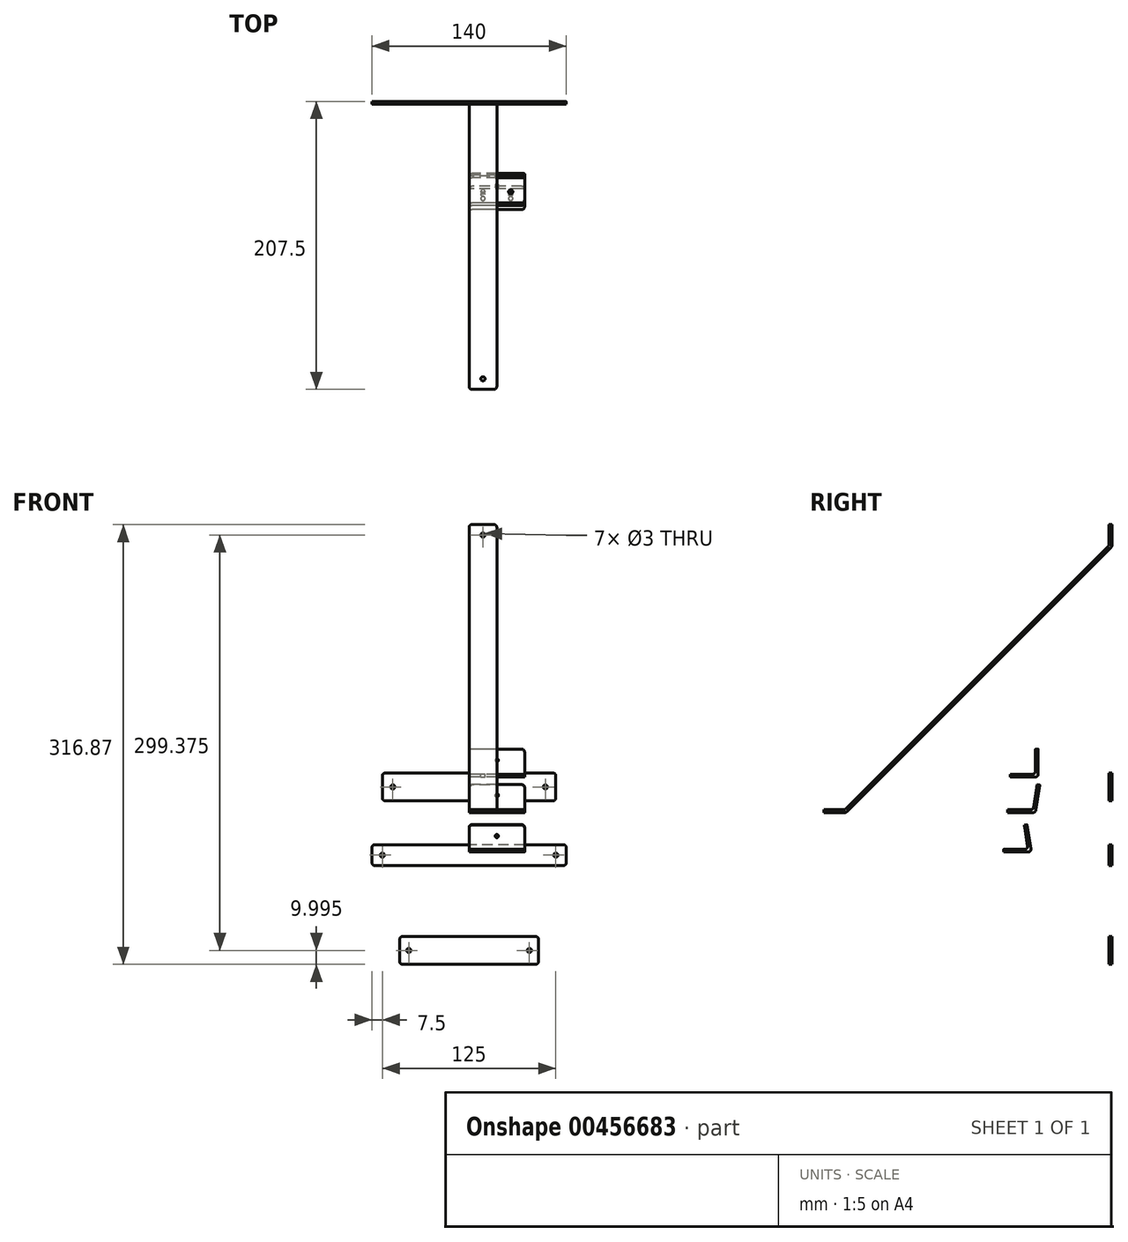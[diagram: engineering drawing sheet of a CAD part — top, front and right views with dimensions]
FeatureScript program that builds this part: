
annotation { "Feature Type Name" : "Feature", "Feature Type Description" : "" }
export const myFeature = defineFeature(function(context is Context, id is Id, definition is map)
    precondition{}
    {
        {
            var Q0;
            Q0=qCreatedBy(makeId("Front.planeOp"),FACE);
            var sketch = newSketch(context, id + "F0", { "sketchPlane" : qUnion([Q0])});
            skLineSegment(sketch, "E0.bottom", {"start": v(62.5, 8.45) * mm, "end": v(-62.5, 8.45) * mm});
            skLineSegment(sketch, "E0.top", {"start": v(62.5, 28.45) * mm, "end": v(-62.5, 28.45) * mm});
            skLineSegment(sketch, "E0.left", {"start": v(62.5, 8.45) * mm, "end": v(62.5, 28.45) * mm});
            skLineSegment(sketch, "E0.right", {"start": v(-62.5, 8.45) * mm, "end": v(-62.5, 28.45) * mm});
            skPoint(sketch, "E0.middle", {"position": v(0, 18.45) * mm});
            skCircle(sketch, "E1", {"center": v(-55, 18.45) * mm, "radius": 1.5 * mm});
            skCircle(sketch, "E2", {"center": v(55, 18.45) * mm, "radius": 1.5 * mm});
            skSolve(sketch);
        }
        {
            var Q0;
            Q0=qSketchRegion(id+"F0",true);
            extrude(context, id + "F1", {"entities" : qUnion([Q0]), "depth" : 2 * mm});
        }
        {
            var Q0;
            Q0=makeQuery(id+"F1.opExtrude","SWEPT_EDGE",EDGE,{"disambiguationData":[OSD([sQuery(id+"F0.wireOp",EDGE,"E0.top"),sQuery(id+"F0.wireOp",EDGE,"E0.right")])]});
            var Q1;
            Q1=makeQuery(id+"F1.opExtrude","SWEPT_EDGE",EDGE,{"disambiguationData":[OSD([sQuery(id+"F0.wireOp",EDGE,"E0.bottom"),sQuery(id+"F0.wireOp",EDGE,"E0.right")])]});
            var Q2;
            Q2=makeQuery(id+"F1.opExtrude","SWEPT_EDGE",EDGE,{"disambiguationData":[OSD([sQuery(id+"F0.wireOp",EDGE,"E0.top"),sQuery(id+"F0.wireOp",EDGE,"E0.left")])]});
            var Q3;
            Q3=makeQuery(id+"F1.opExtrude","SWEPT_EDGE",EDGE,{"disambiguationData":[OSD([sQuery(id+"F0.wireOp",EDGE,"E0.bottom"),sQuery(id+"F0.wireOp",EDGE,"E0.left")])]});
            fillet(context, id + "F2", {"entities" : qUnion([Q0, Q1, Q2, Q3]), "radius" : 2 * mm, "tangentPropagation" : true, "allowEdgeOverflow" : false});
        }
        {
            var Q0;
            Q0=qCreatedBy(makeId("Front.planeOp"),FACE);
            var sketch = newSketch(context, id + "F3", { "sketchPlane" : qUnion([Q0])});
            skLineSegment(sketch, "E3.bottom", {"start": v(70, -38.18) * mm, "end": v(-70, -38.18) * mm});
            skLineSegment(sketch, "E3.top", {"start": v(70, -23.18) * mm, "end": v(-70, -23.18) * mm});
            skLineSegment(sketch, "E3.left", {"start": v(70, -38.18) * mm, "end": v(70, -23.18) * mm});
            skLineSegment(sketch, "E3.right", {"start": v(-70, -38.18) * mm, "end": v(-70, -23.18) * mm});
            skPoint(sketch, "E3.middle", {"position": v(0, -30.68) * mm});
            skCircle(sketch, "E4", {"center": v(-62.5, -30.68) * mm, "radius": 1.5 * mm});
            skCircle(sketch, "E5", {"center": v(62.5, -30.68) * mm, "radius": 1.5 * mm});
            skCircle(sketch, "E6", {"center": v(-43.45, -30.68) * mm, "radius": 1.5 * mm, "construction": true});
            skCircle(sketch, "E7", {"center": v(43.45, -30.68) * mm, "radius": 1.5 * mm, "construction": true});
            skSolve(sketch);
        }
        {
            var Q0;
            Q0=qSketchRegion(id+"F3",true);
            extrude(context, id + "F4", {"entities" : qUnion([Q0]), "depth" : 2 * mm});
        }
        {
            var Q0;
            Q0=makeQuery(id+"F4.opExtrude","SWEPT_EDGE",EDGE,{"disambiguationData":[OSD([sQuery(id+"F3.wireOp",EDGE,"E3.top"),sQuery(id+"F3.wireOp",EDGE,"E3.right")])]});
            var Q1;
            Q1=makeQuery(id+"F4.opExtrude","SWEPT_EDGE",EDGE,{"disambiguationData":[OSD([sQuery(id+"F3.wireOp",EDGE,"E3.bottom"),sQuery(id+"F3.wireOp",EDGE,"E3.right")])]});
            var Q2;
            Q2=makeQuery(id+"F4.opExtrude","SWEPT_EDGE",EDGE,{"disambiguationData":[OSD([sQuery(id+"F3.wireOp",EDGE,"E3.top"),sQuery(id+"F3.wireOp",EDGE,"E3.left")])]});
            var Q3;
            Q3=makeQuery(id+"F4.opExtrude","SWEPT_EDGE",EDGE,{"disambiguationData":[OSD([sQuery(id+"F3.wireOp",EDGE,"E3.bottom"),sQuery(id+"F3.wireOp",EDGE,"E3.left")])]});
            fillet(context, id + "F5", {"entities" : qUnion([Q0, Q1, Q2, Q3]), "radius" : 2 * mm, "tangentPropagation" : true, "allowEdgeOverflow" : false});
        }
        {
            var Q0;
            Q0=qCreatedBy(makeId("Right.planeOp"),FACE);
            var sketch = newSketch(context, id + "F6", { "sketchPlane" : qUnion([Q0])});
            skLineSegment(sketch, "E8.bottom", {"start": v(0, 207.5) * mm, "end": v(-2, 207.5) * mm});
            skLineSegment(sketch, "E8.left", {"start": v(0, 207.5) * mm, "end": v(0, 191.67) * mm});
            skLineSegment(sketch, "E8.right", {"start": v(-2, 207.5) * mm, "end": v(-2, 192.5) * mm});
            skLineSegment(sketch, "E9.bottom", {"start": v(-192.5, 2) * mm, "end": v(-207.5, 2) * mm});
            skLineSegment(sketch, "E9.top", {"start": v(-191.67, 0) * mm, "end": v(-207.5, 0) * mm});
            skLineSegment(sketch, "E9.right", {"start": v(-207.5, 2) * mm, "end": v(-207.5, 0) * mm});
            skLineSegment(sketch, "E10", {"start": v(-2, 192.5) * mm, "end": v(-192.5, 2) * mm});
            skLineSegment(sketch, "E11", {"start": v(0, 200) * mm, "end": v(0, 0) * mm, "construction": true});
            skLineSegment(sketch, "E12", {"start": v(0, 0) * mm, "end": v(-200, 0) * mm, "construction": true});
            skLineSegment(sketch, "E13", {"start": v(0, 191.67) * mm, "end": v(-191.67, 0) * mm});
            skSolve(sketch);
        }
        {
            var Q0;
            Q0=qSketchRegion(id+"F6",true);
            extrude(context, id + "F7", {"entities" : qUnion([Q0]), "depth" : 20 * mm});
        }
        {
            var Q0;
            Q0=makeQuery(id+"F7.opExtrude","SWEPT_FACE",FACE,{"disambiguationData":[OSD([sQuery(id+"F6.wireOp",EDGE,"E8.right")])]});
            var sketch = newSketch(context, id + "F8", { "sketchPlane" : qUnion([Q0])});
            skCircle(sketch, "E14", {"center": v(10, 200) * mm, "radius": 1.5 * mm});
            skSolve(sketch);
        }
        {
            var Q0;
            Q0=makeQuery(id+"F7.opExtrude","SWEPT_FACE",FACE,{"disambiguationData":[OSD([sQuery(id+"F6.wireOp",EDGE,"E9.bottom")])]});
            var sketch = newSketch(context, id + "F9", { "sketchPlane" : qUnion([Q0])});
            skCircle(sketch, "E15", {"center": v(10, -200) * mm, "radius": 1.5 * mm});
            skPoint(sketch, "E15.centerSnap0", {"position": v(10, -192.5) * mm});
            skSolve(sketch);
        }
        {
            var Q0;
            Q0=sQuery(id+"F8.wireOp",VERTEX,"E14.center");
            var Q1;
            Q1=sQuery(id+"F9.wireOp",VERTEX,"E15.center");
            var Q2;
            Q2=makeQuery(id+"F7.opExtrude","SWEPT_BODY",BODY,{"disambiguationData":[OSD([sQuery(id+"F6.wireOp",EDGE,"E8.bottom"),sQuery(id+"F6.wireOp",EDGE,"E8.left"),sQuery(id+"F6.wireOp",EDGE,"E8.right"),sQuery(id+"F6.wireOp",EDGE,"E9.bottom"),sQuery(id+"F6.wireOp",EDGE,"E9.top"),sQuery(id+"F6.wireOp",EDGE,"E9.right"),sQuery(id+"F6.wireOp",EDGE,"E10"),sQuery(id+"F6.wireOp",EDGE,"E13")])]});
            hole(context, id + "F10", {"style" : HoleStyle.SIMPLE, "endStyle" : HoleEndStyle.BLIND, "holeDiameter" : 3 * mm, "holeDepth" : 10 * mm, "tappedDepth" : 12 * mm, "tapClearance" : 3, "locations" : qUnion([Q0, Q1]), "scope" : qUnion([Q2])});
        }
        {
            var Q0;
            Q0=makeQuery(id+"F7.opExtrude","SWEPT_EDGE",EDGE,{"disambiguationData":[OSD([sQuery(id+"F6.wireOp",EDGE,"E8.right"),sQuery(id+"F6.wireOp",EDGE,"E10")])]});
            var Q1;
            Q1=makeQuery(id+"F7.opExtrude","SWEPT_EDGE",EDGE,{"disambiguationData":[OSD([sQuery(id+"F6.wireOp",EDGE,"E8.left"),sQuery(id+"F6.wireOp",EDGE,"E13")])]});
            var Q2;
            Q2=makeQuery(id+"F7.opExtrude","SWEPT_EDGE",EDGE,{"disambiguationData":[OSD([sQuery(id+"F6.wireOp",EDGE,"E9.top"),sQuery(id+"F6.wireOp",EDGE,"E13")])]});
            var Q3;
            Q3=makeQuery(id+"F7.opExtrude","SWEPT_EDGE",EDGE,{"disambiguationData":[OSD([sQuery(id+"F6.wireOp",EDGE,"E9.bottom"),sQuery(id+"F6.wireOp",EDGE,"E10")])]});
            var Q4;
            Q4=makeQuery(id+"F7.opExtrude","CAP_EDGE",EDGE,{"disambiguationData":[OSD([sQuery(id+"F6.wireOp",EDGE,"E8.bottom")])],"isStart":true});
            var Q5;
            Q5=makeQuery(id+"F7.opExtrude","CAP_EDGE",EDGE,{"disambiguationData":[OSD([sQuery(id+"F6.wireOp",EDGE,"E8.bottom")])],"isStart":false});
            var Q6;
            Q6=makeQuery(id+"F7.opExtrude","CAP_EDGE",EDGE,{"disambiguationData":[OSD([sQuery(id+"F6.wireOp",EDGE,"E9.right")])],"isStart":false});
            var Q7;
            Q7=makeQuery(id+"F7.opExtrude","CAP_EDGE",EDGE,{"disambiguationData":[OSD([sQuery(id+"F6.wireOp",EDGE,"E9.right")])],"isStart":true});
            fillet(context, id + "F11", {"entities" : qUnion([Q0, Q1, Q2, Q3, Q4, Q5, Q6, Q7]), "radius" : 2 * mm, "tangentPropagation" : true, "allowEdgeOverflow" : false});
        }
        {
            var Q0;
            Q0=qCreatedBy(makeId("Front.planeOp"),FACE);
            var sketch = newSketch(context, id + "F12", { "sketchPlane" : qUnion([Q0])});
            skLineSegment(sketch, "E16.bottom", {"start": v(50, -109.37) * mm, "end": v(-50, -109.37) * mm});
            skLineSegment(sketch, "E16.top", {"start": v(50, -89.37) * mm, "end": v(-50, -89.37) * mm});
            skLineSegment(sketch, "E16.left", {"start": v(50, -109.37) * mm, "end": v(50, -89.37) * mm});
            skLineSegment(sketch, "E16.right", {"start": v(-50, -109.37) * mm, "end": v(-50, -89.37) * mm});
            skPoint(sketch, "E16.middle", {"position": v(0, -99.37) * mm});
            skCircle(sketch, "E17", {"center": v(-43.45, -99.37) * mm, "radius": 1.5 * mm});
            skCircle(sketch, "E18", {"center": v(43.45, -99.37) * mm, "radius": 1.5 * mm});
            skSolve(sketch);
        }
        {
            var Q0;
            Q0=qSketchRegion(id+"F12",true);
            extrude(context, id + "F13", {"entities" : qUnion([Q0]), "depth" : 2 * mm});
        }
        {
            var Q0;
            Q0=makeQuery(id+"F13.opExtrude","SWEPT_EDGE",EDGE,{"disambiguationData":[OSD([sQuery(id+"F12.wireOp",EDGE,"E16.top"),sQuery(id+"F12.wireOp",EDGE,"E16.right")])]});
            var Q1;
            Q1=makeQuery(id+"F13.opExtrude","SWEPT_EDGE",EDGE,{"disambiguationData":[OSD([sQuery(id+"F12.wireOp",EDGE,"E16.bottom"),sQuery(id+"F12.wireOp",EDGE,"E16.right")])]});
            var Q2;
            Q2=makeQuery(id+"F13.opExtrude","SWEPT_EDGE",EDGE,{"disambiguationData":[OSD([sQuery(id+"F12.wireOp",EDGE,"E16.top"),sQuery(id+"F12.wireOp",EDGE,"E16.left")])]});
            var Q3;
            Q3=makeQuery(id+"F13.opExtrude","SWEPT_EDGE",EDGE,{"disambiguationData":[OSD([sQuery(id+"F12.wireOp",EDGE,"E16.bottom"),sQuery(id+"F12.wireOp",EDGE,"E16.left")])]});
            fillet(context, id + "F14", {"entities" : qUnion([Q0, Q1, Q2, Q3]), "radius" : 2 * mm, "tangentPropagation" : true, "allowEdgeOverflow" : false});
        }
        {
            var Q0;
            Q0=qCreatedBy(makeId("Right.planeOp"),FACE);
            var sketch = newSketch(context, id + "F15", { "sketchPlane" : qUnion([Q0])});
            skLineSegment(sketch, "E19.bottom", {"start": v(-53.14, 45.65) * mm, "end": v(-55.14, 45.65) * mm});
            skLineSegment(sketch, "E19.top", {"start": v(-53.14, 27.65) * mm, "end": v(-55.14, 27.65) * mm});
            skLineSegment(sketch, "E19.left", {"start": v(-53.14, 45.65) * mm, "end": v(-53.14, 27.65) * mm});
            skLineSegment(sketch, "E19.right", {"start": v(-55.14, 45.65) * mm, "end": v(-55.14, 27.65) * mm});
            skLineSegment(sketch, "E20.bottom", {"start": v(-53.14, 27.65) * mm, "end": v(-73.14, 27.65) * mm});
            skLineSegment(sketch, "E20.top", {"start": v(-53.14, 25.65) * mm, "end": v(-73.14, 25.65) * mm});
            skLineSegment(sketch, "E20.left", {"start": v(-53.14, 27.65) * mm, "end": v(-53.14, 25.65) * mm});
            skLineSegment(sketch, "E20.right", {"start": v(-73.14, 27.65) * mm, "end": v(-73.14, 25.65) * mm});
            skSolve(sketch);
        }
        {
            var Q0;
            Q0=qSketchRegion(id+"F15",true);
            extrude(context, id + "F16", {"entities" : qUnion([Q0]), "depth" : 40 * mm});
        }
        {
            var Q0;
            Q0=makeQuery(id+"F16.opExtrude","SWEPT_FACE",FACE,{"disambiguationData":[OSD([sQuery(id+"F15.wireOp",EDGE,"E19.right")])]});
            var sketch = newSketch(context, id + "F17", { "sketchPlane" : qUnion([Q0])});
            skCircle(sketch, "E21", {"center": v(20, 37.65) * mm, "radius": 1.2 * mm});
            skSolve(sketch);
        }
        {
            var Q0;
            Q0=makeQuery(id+"F16.opExtrude","SWEPT_FACE",FACE,{"disambiguationData":[OSD([sQuery(id+"F15.wireOp",EDGE,"E20.bottom")])]});
            var sketch = newSketch(context, id + "F18", { "sketchPlane" : qUnion([Q0])});
            skCircle(sketch, "E22", {"center": v(10, -65.14) * mm, "radius": 1.5 * mm});
            skCircle(sketch, "E23", {"center": v(30, -65.14) * mm, "radius": 1.5 * mm});
            skSolve(sketch);
        }
        {
            var Q0;
            Q0=makeQuery(id+"F16.opExtrude","SWEPT_EDGE",EDGE,{"disambiguationData":[OSD([sQuery(id+"F15.wireOp",EDGE,"E19.right"),sQuery(id+"F15.wireOp",EDGE,"E20.bottom")])]});
            var Q1;
            Q1=makeQuery(id+"F16.opExtrude","SWEPT_EDGE",EDGE,{"disambiguationData":[OSD([sQuery(id+"F15.wireOp",EDGE,"E20.top"),sQuery(id+"F15.wireOp",EDGE,"E20.left")])]});
            var Q2;
            Q2=makeQuery(id+"F16.opExtrude","CAP_EDGE",EDGE,{"disambiguationData":[OSD([sQuery(id+"F15.wireOp",EDGE,"E19.bottom")])],"isStart":true});
            var Q3;
            Q3=makeQuery(id+"F16.opExtrude","CAP_EDGE",EDGE,{"disambiguationData":[OSD([sQuery(id+"F15.wireOp",EDGE,"E19.bottom")])],"isStart":false});
            var Q4;
            Q4=makeQuery(id+"F16.opExtrude","CAP_EDGE",EDGE,{"disambiguationData":[OSD([sQuery(id+"F15.wireOp",EDGE,"E20.right")])],"isStart":false});
            var Q5;
            Q5=makeQuery(id+"F16.opExtrude","CAP_EDGE",EDGE,{"disambiguationData":[OSD([sQuery(id+"F15.wireOp",EDGE,"E20.right")])],"isStart":true});
            fillet(context, id + "F19", {"entities" : qUnion([Q0, Q1, Q2, Q3, Q4, Q5]), "radius" : 2 * mm, "tangentPropagation" : true, "allowEdgeOverflow" : false});
        }
        {
            var Q0;
            Q0=qCreatedBy(makeId("Right.planeOp"),FACE);
            var sketch = newSketch(context, id + "F20", { "sketchPlane" : qUnion([Q0])});
            skLineSegment(sketch, "E24.top", {"start": v(-75.09, 0) * mm, "end": v(-55.09, 0) * mm});
            skLineSegment(sketch, "E24.left", {"start": v(-75.09, 2) * mm, "end": v(-75.09, 0) * mm});
            skLineSegment(sketch, "E25", {"start": v(-75.09, 2) * mm, "end": v(-56.8, 2) * mm});
            skLineSegment(sketch, "E26", {"start": v(-56.8, 2) * mm, "end": v(-53.93, 20.07) * mm});
            skLineSegment(sketch, "E27", {"start": v(-53.93, 20.07) * mm, "end": v(-51.96, 19.75) * mm});
            skLineSegment(sketch, "E28", {"start": v(-51.96, 19.75) * mm, "end": v(-55.09, 0) * mm});
            skPoint(sketch, "E29", {"position": v(-53.16, 12.15) * mm});
            skLineSegment(sketch, "E30", {"start": v(-55.09, 0) * mm, "end": v(-55.5, -2.64) * mm, "construction": true});
            skLineSegment(sketch, "E31", {"start": v(-55.5, -2.64) * mm, "end": v(-53.53, -2.95) * mm, "construction": true});
            skLineSegment(sketch, "E32", {"start": v(-53.53, -2.95) * mm, "end": v(-50.78, 14.39) * mm, "construction": true});
            skPoint(sketch, "E33", {"position": v(-51.18, 11.86) * mm});
            skLineSegment(sketch, "E34", {"start": v(-52.3, -3) * mm, "end": v(-61.2, -3) * mm, "construction": true});
            skSolve(sketch);
        }
        {
            var Q0;
            Q0=qSketchRegion(id+"F20",true);
            extrude(context, id + "F21", {"entities" : qUnion([Q0]), "depth" : 40 * mm});
        }
        {
            var Q0;
            Q0=makeQuery(id+"F21.opExtrude","SWEPT_FACE",FACE,{"disambiguationData":[OSD([sQuery(id+"F20.wireOp",EDGE,"E28")])]});
            var sketch = newSketch(context, id + "F22", { "sketchPlane" : qUnion([Q0])});
            skCircle(sketch, "E35", {"center": v(-20, 3.68) * mm, "radius": 1.2 * mm});
            skSolve(sketch);
        }
        {
            var Q0;
            Q0=makeQuery(id+"F21.opExtrude","SWEPT_FACE",FACE,{"disambiguationData":[OSD([sQuery(id+"F20.wireOp",EDGE,"E25")])]});
            var sketch = newSketch(context, id + "F23", { "sketchPlane" : qUnion([Q0])});
            skCircle(sketch, "E36", {"center": v(10, -67.09) * mm, "radius": 1.5 * mm});
            skCircle(sketch, "E37", {"center": v(30, -67.09) * mm, "radius": 1.5 * mm});
            skSolve(sketch);
        }
        {
            var Q0;
            Q0=makeQuery(id+"F21.opExtrude","SWEPT_EDGE",EDGE,{"disambiguationData":[OSD([sQuery(id+"F20.wireOp",EDGE,"E25"),sQuery(id+"F20.wireOp",EDGE,"E26")])]});
            var Q1;
            Q1=makeQuery(id+"F21.opExtrude","SWEPT_EDGE",EDGE,{"disambiguationData":[OSD([sQuery(id+"F20.wireOp",EDGE,"E24.top"),sQuery(id+"F20.wireOp",EDGE,"E28")])]});
            var Q2;
            Q2=makeQuery(id+"F21.opExtrude","CAP_EDGE",EDGE,{"disambiguationData":[OSD([sQuery(id+"F20.wireOp",EDGE,"E27")])],"isStart":true});
            var Q3;
            Q3=makeQuery(id+"F21.opExtrude","CAP_EDGE",EDGE,{"disambiguationData":[OSD([sQuery(id+"F20.wireOp",EDGE,"E24.left")])],"isStart":true});
            var Q4;
            Q4=makeQuery(id+"F21.opExtrude","CAP_EDGE",EDGE,{"disambiguationData":[OSD([sQuery(id+"F20.wireOp",EDGE,"E24.left")])],"isStart":false});
            var Q5;
            Q5=makeQuery(id+"F21.opExtrude","CAP_EDGE",EDGE,{"disambiguationData":[OSD([sQuery(id+"F20.wireOp",EDGE,"E27")])],"isStart":false});
            fillet(context, id + "F24", {"entities" : qUnion([Q0, Q1, Q2, Q3, Q4, Q5]), "radius" : 2 * mm, "tangentPropagation" : true, "allowEdgeOverflow" : false});
        }
        {
            var Q0;
            Q0=qCreatedBy(makeId("Right.planeOp"),FACE);
            var sketch = newSketch(context, id + "F25", { "sketchPlane" : qUnion([Q0])});
            skLineSegment(sketch, "E38.top", {"start": v(-78.05, -28.5) * mm, "end": v(-58.05, -28.5) * mm});
            skLineSegment(sketch, "E38.left", {"start": v(-78.05, -26.5) * mm, "end": v(-78.05, -28.5) * mm});
            skLineSegment(sketch, "E39", {"start": v(-78.05, -26.5) * mm, "end": v(-60.4, -26.5) * mm});
            skLineSegment(sketch, "E40", {"start": v(-60.4, -26.5) * mm, "end": v(-63.16, -9.06) * mm});
            skLineSegment(sketch, "E41", {"start": v(-63.16, -9.06) * mm, "end": v(-61.18, -8.74) * mm});
            skLineSegment(sketch, "E42", {"start": v(-61.18, -8.74) * mm, "end": v(-58.05, -28.5) * mm});
            skLineSegment(sketch, "E43", {"start": v(-58.05, -28.5) * mm, "end": v(-57.58, -31.46) * mm, "construction": true});
            skLineSegment(sketch, "E44", {"start": v(-57.58, -31.46) * mm, "end": v(-55.6, -31.15) * mm, "construction": true});
            skLineSegment(sketch, "E45", {"start": v(-55.6, -31.15) * mm, "end": v(-58.2, -14.75) * mm, "construction": true});
            skLineSegment(sketch, "E46", {"start": v(-50.6, -31.5) * mm, "end": v(-63.36, -31.5) * mm, "construction": true});
            skPoint(sketch, "E47", {"position": v(-59.93, -16.64) * mm});
            skPoint(sketch, "E48", {"position": v(-57.95, -16.33) * mm});
            skSolve(sketch);
        }
        {
            var Q0;
            Q0=qSketchRegion(id+"F25",true);
            extrude(context, id + "F26", {"entities" : qUnion([Q0]), "depth" : 40 * mm});
        }
        {
            var Q0;
            Q0=makeQuery(id+"F26.opExtrude","SWEPT_FACE",FACE,{"disambiguationData":[OSD([sQuery(id+"F25.wireOp",EDGE,"E39")])]});
            var sketch = newSketch(context, id + "F27", { "sketchPlane" : qUnion([Q0])});
            skCircle(sketch, "E49", {"center": v(10, -70.05) * mm, "radius": 1.5 * mm});
            skCircle(sketch, "E50", {"center": v(30, -70.05) * mm, "radius": 1.5 * mm});
            skSolve(sketch);
        }
        {
            var Q0;
            Q0=makeQuery(id+"F26.opExtrude","SWEPT_FACE",FACE,{"disambiguationData":[OSD([sQuery(id+"F25.wireOp",EDGE,"E40")])]});
            var sketch = newSketch(context, id + "F28", { "sketchPlane" : qUnion([Q0])});
            skCircle(sketch, "E51", {"center": v(20, -7.06) * mm, "radius": 1.2 * mm});
            skSolve(sketch);
        }
        {
            var Q0;
            Q0=sQuery(id+"F18.wireOp",VERTEX,"E22.center");
            var Q1;
            Q1=sQuery(id+"F18.wireOp",VERTEX,"E23.center");
            var Q2;
            Q2=sQuery(id+"F23.wireOp",VERTEX,"E37.center");
            var Q3;
            Q3=sQuery(id+"F23.wireOp",VERTEX,"E36.center");
            var Q4;
            Q4=sQuery(id+"F27.wireOp",VERTEX,"E49.center");
            var Q5;
            Q5=sQuery(id+"F27.wireOp",VERTEX,"E50.center");
            var Q6;
            Q6=makeQuery(id+"F16.opExtrude","SWEPT_BODY",BODY,{"disambiguationData":[OSD([sQuery(id+"F15.wireOp",EDGE,"E19.bottom"),sQuery(id+"F15.wireOp",EDGE,"E19.left"),sQuery(id+"F15.wireOp",EDGE,"E19.right"),sQuery(id+"F15.wireOp",EDGE,"E20.bottom"),sQuery(id+"F15.wireOp",EDGE,"E20.top"),sQuery(id+"F15.wireOp",EDGE,"E20.left"),sQuery(id+"F15.wireOp",EDGE,"E20.right")])]});
            var Q7;
            Q7=makeQuery(id+"F21.opExtrude","SWEPT_BODY",BODY,{"disambiguationData":[OSD([sQuery(id+"F20.wireOp",EDGE,"E24.top"),sQuery(id+"F20.wireOp",EDGE,"E24.left"),sQuery(id+"F20.wireOp",EDGE,"E25"),sQuery(id+"F20.wireOp",EDGE,"E26"),sQuery(id+"F20.wireOp",EDGE,"E27"),sQuery(id+"F20.wireOp",EDGE,"E28")])]});
            var Q8;
            Q8=makeQuery(id+"F26.opExtrude","SWEPT_BODY",BODY,{"disambiguationData":[OSD([sQuery(id+"F25.wireOp",EDGE,"E38.top"),sQuery(id+"F25.wireOp",EDGE,"E38.left"),sQuery(id+"F25.wireOp",EDGE,"E39"),sQuery(id+"F25.wireOp",EDGE,"E40"),sQuery(id+"F25.wireOp",EDGE,"E41"),sQuery(id+"F25.wireOp",EDGE,"E42")])]});
            hole(context, id + "F29", {"style" : HoleStyle.SIMPLE, "endStyle" : HoleEndStyle.BLIND, "holeDiameter" : 3 * mm, "holeDepth" : 10 * mm, "tappedDepth" : 12 * mm, "tapClearance" : 3, "locations" : qUnion([Q0, Q1, Q2, Q3, Q4, Q5]), "scope" : qUnion([Q6, Q7, Q8])});
        }
        {
            var Q0;
            Q0=sQuery(id+"F17.wireOp",VERTEX,"E21.center");
            var Q1;
            Q1=sQuery(id+"F22.wireOp",VERTEX,"E35.center");
            var Q2;
            Q2=sQuery(id+"F28.wireOp",VERTEX,"E51.center");
            var Q3;
            Q3=makeQuery(id+"F16.opExtrude","SWEPT_BODY",BODY,{"disambiguationData":[OSD([sQuery(id+"F15.wireOp",EDGE,"E19.bottom"),sQuery(id+"F15.wireOp",EDGE,"E19.left"),sQuery(id+"F15.wireOp",EDGE,"E19.right"),sQuery(id+"F15.wireOp",EDGE,"E20.bottom"),sQuery(id+"F15.wireOp",EDGE,"E20.top"),sQuery(id+"F15.wireOp",EDGE,"E20.left"),sQuery(id+"F15.wireOp",EDGE,"E20.right")])]});
            var Q4;
            Q4=makeQuery(id+"F21.opExtrude","SWEPT_BODY",BODY,{"disambiguationData":[OSD([sQuery(id+"F20.wireOp",EDGE,"E24.top"),sQuery(id+"F20.wireOp",EDGE,"E24.left"),sQuery(id+"F20.wireOp",EDGE,"E25"),sQuery(id+"F20.wireOp",EDGE,"E26"),sQuery(id+"F20.wireOp",EDGE,"E27"),sQuery(id+"F20.wireOp",EDGE,"E28")])]});
            var Q5;
            Q5=makeQuery(id+"F26.opExtrude","SWEPT_BODY",BODY,{"disambiguationData":[OSD([sQuery(id+"F25.wireOp",EDGE,"E38.top"),sQuery(id+"F25.wireOp",EDGE,"E38.left"),sQuery(id+"F25.wireOp",EDGE,"E39"),sQuery(id+"F25.wireOp",EDGE,"E40"),sQuery(id+"F25.wireOp",EDGE,"E41"),sQuery(id+"F25.wireOp",EDGE,"E42")])]});
            hole(context, id + "F30", {"style" : HoleStyle.SIMPLE, "endStyle" : HoleEndStyle.BLIND, "holeDiameter" : 2.4 * mm, "holeDepth" : 10 * mm, "tappedDepth" : 12 * mm, "tapClearance" : 3, "locations" : qUnion([Q0, Q1, Q2]), "scope" : qUnion([Q3, Q4, Q5])});
        }
        {
            var Q0;
            Q0=makeQuery(id+"F26.opExtrude","SWEPT_EDGE",EDGE,{"disambiguationData":[OSD([sQuery(id+"F25.wireOp",EDGE,"E39"),sQuery(id+"F25.wireOp",EDGE,"E40")])]});
            var Q1;
            Q1=makeQuery(id+"F26.opExtrude","SWEPT_EDGE",EDGE,{"disambiguationData":[OSD([sQuery(id+"F25.wireOp",EDGE,"E38.top"),sQuery(id+"F25.wireOp",EDGE,"E42")])]});
            var Q2;
            Q2=makeQuery(id+"F26.opExtrude","CAP_EDGE",EDGE,{"disambiguationData":[OSD([sQuery(id+"F25.wireOp",EDGE,"E41")])],"isStart":false});
            var Q3;
            Q3=makeQuery(id+"F26.opExtrude","CAP_EDGE",EDGE,{"disambiguationData":[OSD([sQuery(id+"F25.wireOp",EDGE,"E41")])],"isStart":true});
            var Q4;
            Q4=makeQuery(id+"F26.opExtrude","CAP_EDGE",EDGE,{"disambiguationData":[OSD([sQuery(id+"F25.wireOp",EDGE,"E38.left")])],"isStart":true});
            var Q5;
            Q5=makeQuery(id+"F26.opExtrude","CAP_EDGE",EDGE,{"disambiguationData":[OSD([sQuery(id+"F25.wireOp",EDGE,"E38.left")])],"isStart":false});
            fillet(context, id + "F31", {"entities" : qUnion([Q0, Q1, Q2, Q3, Q4, Q5]), "radius" : 2 * mm, "tangentPropagation" : true, "allowEdgeOverflow" : false});
        }
    });
